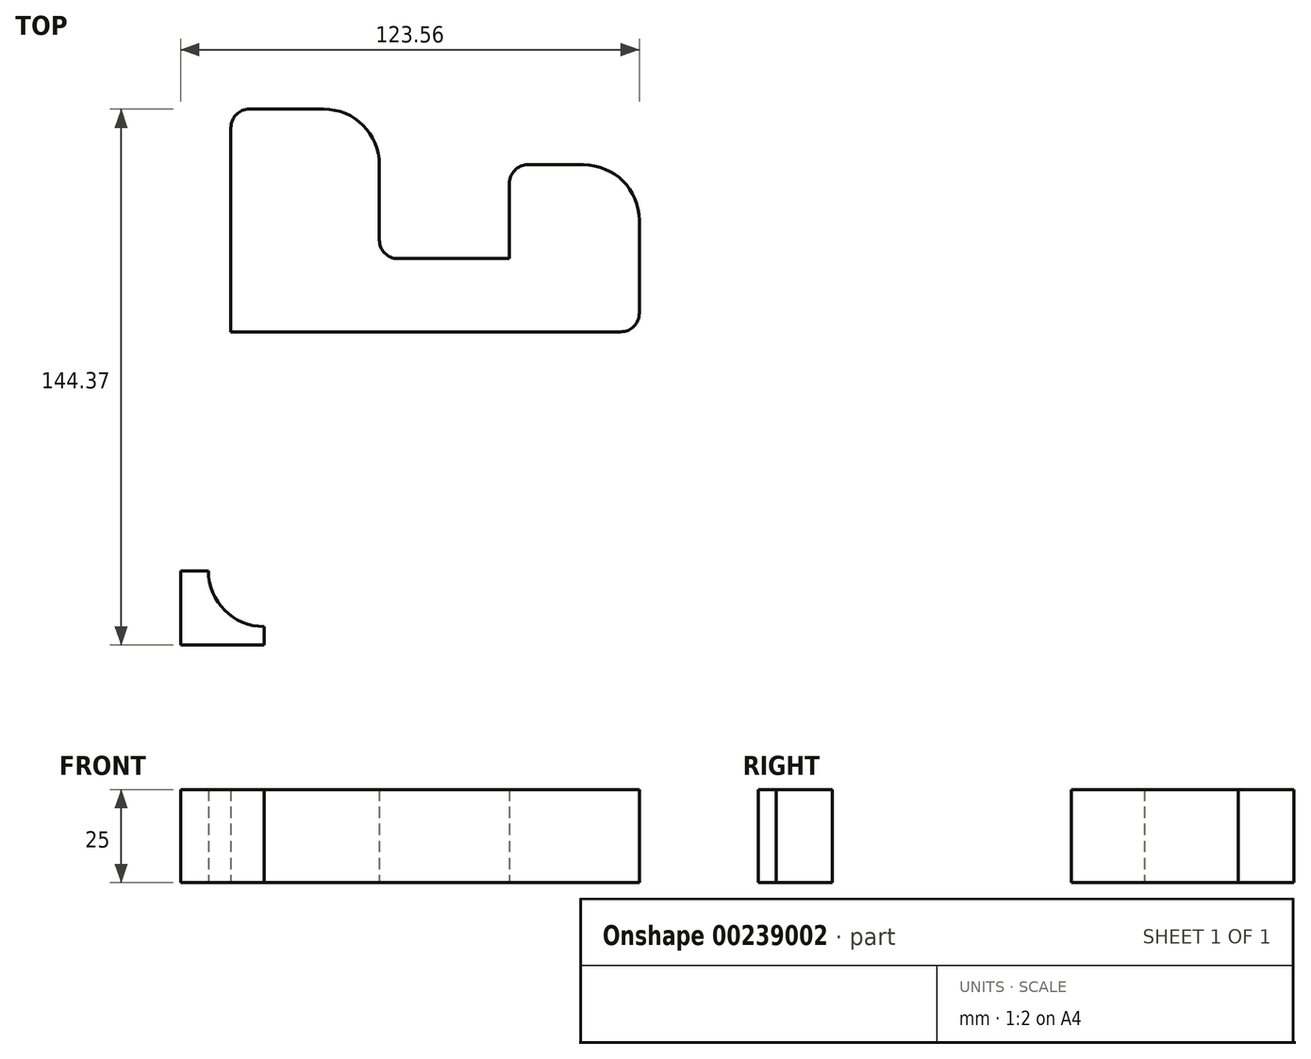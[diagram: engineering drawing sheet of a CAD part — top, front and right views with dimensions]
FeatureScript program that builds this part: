
annotation { "Feature Type Name" : "Feature", "Feature Type Description" : "" }
export const myFeature = defineFeature(function(context is Context, id is Id, definition is map)
    precondition{}
    {
        {
            var Q0;
            Q0=qCreatedBy(makeId("Top.planeOp"),FACE);
            var sketch = newSketch(context, id + "F0", { "sketchPlane" : qUnion([Q0])});
            skLineSegment(sketch, "E0", {"start": v(-32.69, 34) * mm, "end": v(-32.69, -21) * mm});
            skLineSegment(sketch, "E1", {"start": v(-32.69, -21) * mm, "end": v(72.31, -21) * mm});
            skLineSegment(sketch, "E2", {"start": v(77.31, -16) * mm, "end": v(77.31, 9) * mm});
            skLineSegment(sketch, "E3", {"start": v(62.31, 24) * mm, "end": v(47.31, 24) * mm});
            skLineSegment(sketch, "E4", {"start": v(42.31, -1.29) * mm, "end": v(12.31, -1.29) * mm});
            skLineSegment(sketch, "E5", {"start": v(42.31, -1.29) * mm, "end": v(42.31, 19) * mm});
            skLineSegment(sketch, "E6", {"start": v(7.31, 3.71) * mm, "end": v(7.31, 24) * mm});
            skLineSegment(sketch, "E7", {"start": v(-27.69, 39) * mm, "end": v(-7.69, 39) * mm});
            skPoint(sketch, "E8.visualSharp", {"position": v(77.31, -21) * mm});
            skArc(sketch, "E8.filletArc", {"start": v(72.31, -21) * mm, "mid": v(75.85, -19.53) * mm, "end": v(77.31, -16) * mm});
            skPoint(sketch, "E9.visualSharp", {"position": v(77.31, 24) * mm});
            skArc(sketch, "E9.filletArc", {"start": v(77.31, 9) * mm, "mid": v(72.92, 19.61) * mm, "end": v(62.31, 24) * mm});
            skPoint(sketch, "E10.visualSharp", {"position": v(42.31, 24) * mm});
            skArc(sketch, "E10.filletArc", {"start": v(47.31, 24) * mm, "mid": v(43.78, 22.54) * mm, "end": v(42.31, 19) * mm});
            skPoint(sketch, "E11.visualSharp", {"position": v(7.31, -1.29) * mm});
            skArc(sketch, "E11.filletArc", {"start": v(7.31, 3.71) * mm, "mid": v(8.78, 0.17) * mm, "end": v(12.31, -1.29) * mm});
            skPoint(sketch, "E12.visualSharp", {"position": v(7.31, 39) * mm});
            skArc(sketch, "E12.filletArc", {"start": v(7.31, 24) * mm, "mid": v(2.92, 34.61) * mm, "end": v(-7.69, 39) * mm});
            skPoint(sketch, "E13.visualSharp", {"position": v(-32.69, 39) * mm});
            skArc(sketch, "E13.filletArc", {"start": v(-27.69, 39) * mm, "mid": v(-31.22, 37.54) * mm, "end": v(-32.69, 34) * mm});
            skLineSegment(sketch, "E14", {"start": v(-46.25, -105.36) * mm, "end": v(18.75, -105.36) * mm});
            skLineSegment(sketch, "E15", {"start": v(28.75, -95.36) * mm, "end": v(28.75, -45.36) * mm});
            skLineSegment(sketch, "E16", {"start": v(28.75, -45.36) * mm, "end": v(-46.25, -75.36) * mm});
            skLineSegment(sketch, "E17", {"start": v(-46.25, -75.36) * mm, "end": v(-46.25, -105.36) * mm});
            skPoint(sketch, "E18.visualSharp", {"position": v(28.75, -105.36) * mm});
            skArc(sketch, "E18.filletArc", {"start": v(18.75, -105.36) * mm, "mid": v(25.82, -102.43) * mm, "end": v(28.75, -95.36) * mm});
            skLineSegment(sketch, "E19", {"start": v(-46.25, -105.36) * mm, "end": v(-23.75, -105.36) * mm});
            skLineSegment(sketch, "E20", {"start": v(-23.75, -105.36) * mm, "end": v(-46.25, -105.36) * mm});
            skLineSegment(sketch, "E21", {"start": v(-58.15, -105.42) * mm, "end": v(-58.15, -85.42) * mm, "construction": true});
            skLineSegment(sketch, "E22", {"start": v(-23.75, -105.36) * mm, "end": v(-23.75, -85.42) * mm});
            skLineSegment(sketch, "E23", {"start": v(-23.75, -85.42) * mm, "end": v(-58.15, -85.42) * mm});
            skCircle(sketch, "E24", {"center": v(-23.75, -85.42) * mm, "radius": 15 * mm});
            skSolve(sketch);
        }
        {
            var Q0;
            Q0=makeQuery(id+"F0.imprint","IMPRINT",FACE,{"disambiguationData":[TD([[makeQuery(id+"F0.imprint","IMPRINT",EDGE,{"derivedFrom":sQuery(id+"F0.wireOp",EDGE,"E0")}),1.0]])]});
            var Q1;
            {var subQ8=sQuery(id+"F0.wireOp",EDGE,"E14");Q1=makeQuery(id+"F0.imprint","IMPRINT",FACE,{"disambiguationData":[TD([[makeQuery(id+"F0.imprint","IMPRINT",EDGE,{"derivedFrom":subQ8}),1.0]])]});}
            var Q2;
            {var subQ6=sQuery(id+"F0.wireOp",EDGE,"E20");Q2=makeQuery(id+"F0.imprint","IMPRINT",FACE,{"disambiguationData":[TD([[makeQuery(id+"F0.imprint","IMPRINT",EDGE,{"derivedFrom":subQ6}),-1.0]])]});}
            extrude(context, id + "F1", {"entities" : qUnion([Q0, Q1, Q2]), "depth" : 25 * mm});
        }
    });
